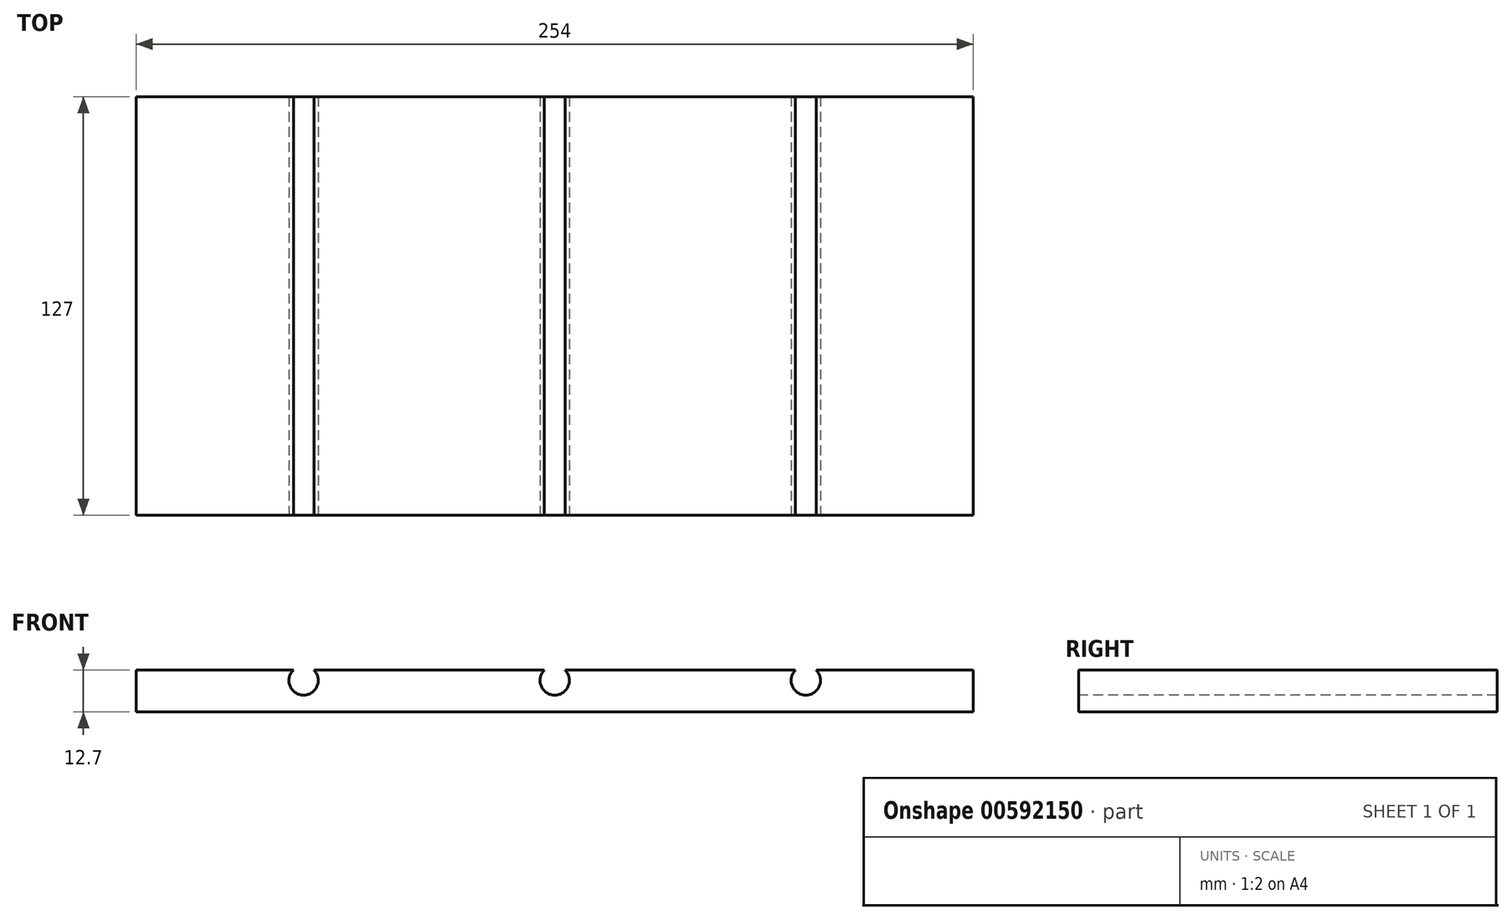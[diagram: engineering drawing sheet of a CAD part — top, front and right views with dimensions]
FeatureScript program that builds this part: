
annotation { "Feature Type Name" : "Feature", "Feature Type Description" : "" }
export const myFeature = defineFeature(function(context is Context, id is Id, definition is map)
    precondition{}
    {
        {
            var Q0;
            Q0=qCreatedBy(makeId("Front.planeOp"),FACE);
            var sketch = newSketch(context, id + "F0", { "sketchPlane" : qUnion([Q0])});
            skLineSegment(sketch, "E0.bottom", {"start": v(0, 0) * mm, "end": v(254, 0) * mm});
            skLineSegment(sketch, "E0.top", {"start": v(0, 12.7) * mm, "end": v(47.69, 12.7) * mm});
            skLineSegment(sketch, "E0.left", {"start": v(0, 0) * mm, "end": v(0, 12.7) * mm});
            skLineSegment(sketch, "E0.right", {"start": v(254, 0) * mm, "end": v(254, 12.7) * mm});
            skArc(sketch, "E1", {"start": v(47.69, 12.7) * mm, "mid": v(50.8, 5.08) * mm, "end": v(53.91, 12.7) * mm});
            skLineSegment(sketch, "E2.trimOffspring", {"start": v(53.91, 12.7) * mm, "end": v(123.89, 12.7) * mm});
            skArc(sketch, "E3", {"start": v(123.89, 12.7) * mm, "mid": v(127, 5.08) * mm, "end": v(130.11, 12.7) * mm});
            skArc(sketch, "E4", {"start": v(200.09, 12.7) * mm, "mid": v(203.2, 5.08) * mm, "end": v(206.31, 12.7) * mm});
            skLineSegment(sketch, "E5.trimOffspring", {"start": v(130.11, 12.7) * mm, "end": v(200.09, 12.7) * mm});
            skLineSegment(sketch, "E6.trimOffspring", {"start": v(206.31, 12.7) * mm, "end": v(254, 12.7) * mm});
            skSolve(sketch);
        }
        {
            var Q0;
            Q0 = qSketchRegion(id + "F0", true);
            extrude(context, id + "F1", {"entities" : qUnion([Q0]), "oppositeDirection" : true, "depth" : 127 * mm, "offsetDistance" : 25.4 * mm});
        }
    });
